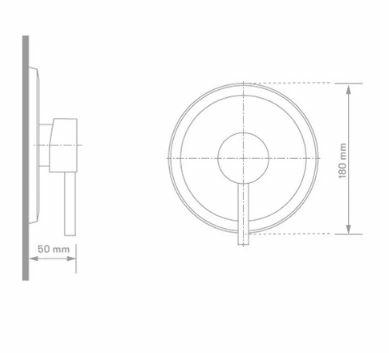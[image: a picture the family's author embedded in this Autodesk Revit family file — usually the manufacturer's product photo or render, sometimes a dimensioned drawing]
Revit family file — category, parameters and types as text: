
# Revit family: 01-2456-11 PORTACEPILLOS METALICO QUADRA
name_source: partatom
category: Plumbing Fixtures
revit_build: Autodesk Revit 2018 (Build: 20170223_1515(x64)
units: mm (PartAtom-declared; Revit-internal decimal feet)

## family parameters
Cut with Voids When Loaded = No
Host = Face
OmniClass Number = 23.31.11.00
Part Type = Normal
Room Calculation Point = No
Round Connector Dimension = Use Diameter
Shared = No

## types (1)
- 01-2456-11
    Alto = 95 mm
    Ancho = 117 mm
    Brazo Portacepillos = Metal Laton Cromado
    CW Connection = Yes
    Default Elevation = 0 mm  [stored 0 ft]
    Description = PORTACEPILLOS
    Diametro vaso = 68 mm
    HW Connection = Yes
    Link Ficha Tecnica = http://infotecnica.gricol.com
    Manufacturer = Gricol
    Model = 01-2456-11
    Product Name = PORTACEPILLOS METALICO QUADRA
    Profundidad = 75 mm
    Soporte = Metal Laton Cromado
    Type Image = PORTACEPILLOS METALICO QUADRA FOTO.jpg
    URL = https://www.gricol.com
    Vaso Portacepillos = Vidrio Esmerilado
    Vent Connection = No
    Waste Connection = No

note: [stored X ft] marks values corroborated as IEEE doubles in the binary element streams (Revit-internal decimal feet)

## geometry (parser evidence)
native form markers: Blend x2, Sweep x4
no freeform markers — native parametric forms only
